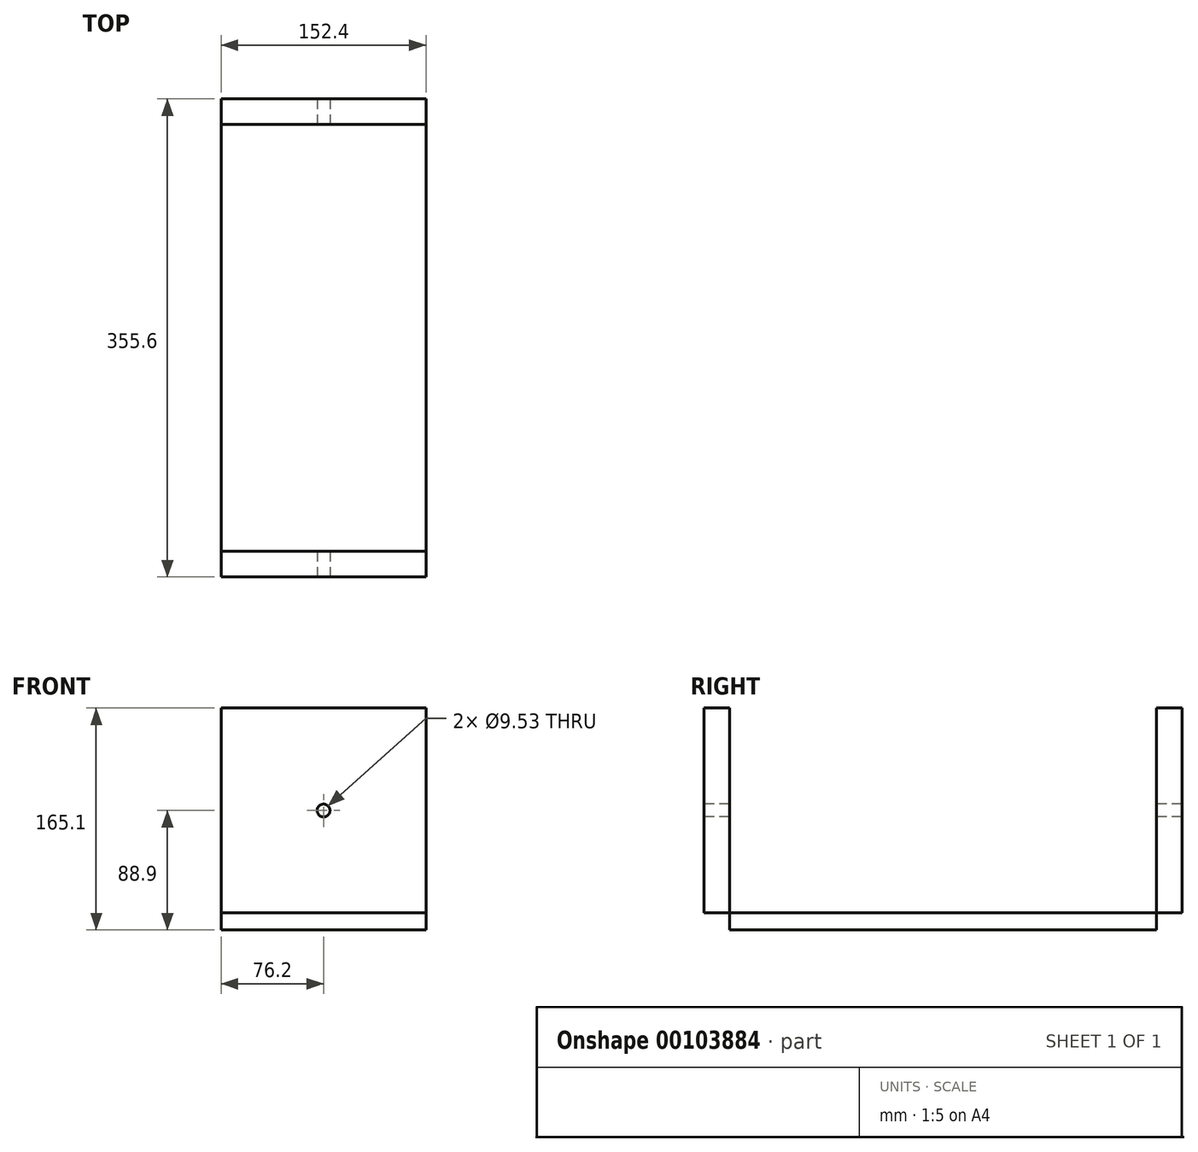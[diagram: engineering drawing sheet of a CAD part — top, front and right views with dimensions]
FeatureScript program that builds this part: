
annotation { "Feature Type Name" : "Feature", "Feature Type Description" : "" }
export const myFeature = defineFeature(function(context is Context, id is Id, definition is map)
    precondition{}
    {
        {
            var Q0;
            Q0=qCreatedBy(makeId("Right.planeOp"),FACE);
            var sketch = newSketch(context, id + "F0", { "sketchPlane" : qUnion([Q0])});
            skLineSegment(sketch, "E0.bottom", {"start": v(0, 0) * mm, "end": v(19.05, 0) * mm});
            skLineSegment(sketch, "E0.top", {"start": v(0, 165.1) * mm, "end": v(19.05, 165.1) * mm});
            skLineSegment(sketch, "E0.left", {"start": v(0, 0) * mm, "end": v(0, 165.1) * mm});
            skLineSegment(sketch, "E0.right", {"start": v(19.05, 0) * mm, "end": v(19.05, 165.1) * mm});
            skLineSegment(sketch, "E1.bottom", {"start": v(0, 0) * mm, "end": v(355.6, 0) * mm});
            skLineSegment(sketch, "E1.top", {"start": v(0, 12.7) * mm, "end": v(355.6, 12.7) * mm});
            skLineSegment(sketch, "E1.left", {"start": v(0, 0) * mm, "end": v(0, 12.7) * mm});
            skLineSegment(sketch, "E1.right", {"start": v(355.6, 0) * mm, "end": v(355.6, 12.7) * mm});
            skLineSegment(sketch, "E2.bottom", {"start": v(355.6, 0) * mm, "end": v(336.55, 0) * mm});
            skLineSegment(sketch, "E2.top", {"start": v(355.6, 165.1) * mm, "end": v(336.55, 165.1) * mm});
            skLineSegment(sketch, "E2.left", {"start": v(355.6, 0) * mm, "end": v(355.6, 165.1) * mm});
            skLineSegment(sketch, "E2.right", {"start": v(336.55, 0) * mm, "end": v(336.55, 165.1) * mm});
            skSolve(sketch);
        }
        {
            var Q0;
            {var subQ0=sQuery(id+"F0.wireOp",EDGE,"E0.top");Q0=makeQuery(id+"F0.imprint","IMPRINT",FACE,{"disambiguationData":[TD([[makeQuery(id+"F0.imprint","IMPRINT",EDGE,{"derivedFrom":subQ0}),-1.0]])]});}
            var Q1;
            {var subQ5=sQuery(id+"F0.wireOp",EDGE,"E1.left");Q1=makeQuery(id+"F0.imprint","IMPRINT",FACE,{"disambiguationData":[TD([[makeQuery(id+"F0.imprint","IMPRINT",EDGE,{"derivedFrom":subQ5}),-1.0]])]});}
            var Q2;
            {var subQ0=sQuery(id+"F0.wireOp",EDGE,"E1.bottom");var subQ1=sQuery(id+"F0.wireOp",EDGE,"E0.right");var subQ2=makeQuery(id+"F0.imprint","INTERSECT",VERTEX,{"derivedFrom":[subQ1,subQ0]});Q2=makeQuery(id+"F0.imprint","IMPRINT",FACE,{"disambiguationData":[TD([[makeQuery(id+"F0.imprint","IMPRINT",EDGE,{"disambiguationData":[TD([[subQ2,-1.0]])],"derivedFrom":subQ1}),-1.0]])]});}
            var Q3;
            {var subQ5=sQuery(id+"F0.wireOp",EDGE,"E2.top");Q3=makeQuery(id+"F0.imprint","IMPRINT",FACE,{"disambiguationData":[TD([[makeQuery(id+"F0.imprint","IMPRINT",EDGE,{"derivedFrom":subQ5}),1.0]])]});}
            var Q4;
            {var subQ5=sQuery(id+"F0.wireOp",EDGE,"E2.bottom");Q4=makeQuery(id+"F0.imprint","IMPRINT",FACE,{"disambiguationData":[TD([[makeQuery(id+"F0.imprint","IMPRINT",EDGE,{"derivedFrom":subQ5}),-1.0]])]});}
            extrude(context, id + "F1", {"entities" : qUnion([Q0, Q1, Q2, Q3, Q4]), "depth" : 152.4 * mm});
        }
        {
            var Q0;
            Q0=qCreatedBy(makeId("Front.planeOp"),FACE);
            var sketch = newSketch(context, id + "F2", { "sketchPlane" : qUnion([Q0])});
            skCircle(sketch, "E3", {"center": v(76.2, 88.9) * mm, "radius": 4.76 * mm});
            skSolve(sketch);
        }
        {
            var Q0;
            Q0=makeQuery(id+"F2.imprint","IMPRINT",FACE,{"disambiguationData":[TD([[makeQuery(id+"F2.imprint","IMPRINT",EDGE,{"derivedFrom":sQuery(id+"F2.wireOp",EDGE,"E3")}),1.0]])]});
            extrude(context, id + "F3", {"entities" : qUnion([Q0]), "operationType" : NewBodyOperationType.REMOVE, "oppositeDirection" : true, "depth" : 406.4 * mm});
        }
    });
